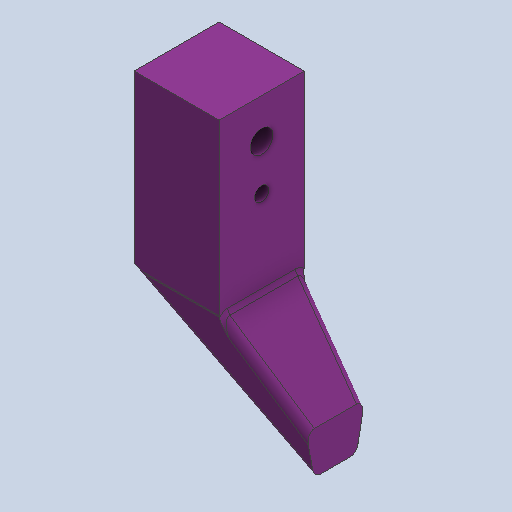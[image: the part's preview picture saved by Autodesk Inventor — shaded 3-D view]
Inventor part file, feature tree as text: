
AUTODESK INVENTOR PART (.ipt)
format: ipt  version: 2025.1 (Build 291241020, 241B)  size: 309,248 bytes
history: native  units: in
note: dims shown in document units (in); Inventor stores cm internally (conversion verified against a paired STEP export)
features: extrude x4, sketch x4, fillet x1
ambient origin geometry x8: Origin, YZ Plane, XZ Plane, XY Plane, X Axis, Y Axis, Z Axis, Center Point
bodies: Solid1 (feature_tree)
feature tree (9):
  extrude  "Extrusion1"  Depth=1.5in
  extrude  "Extrusion2"  Depth=2.0in
  extrude  "Extrusion3"  Depth=1.5in TaperAngle=0.0deg
  fillet  "Fillet1"  Radius=0.375in
  extrude  "Extrusion4"  Depth=0.125in
  sketch  "Sketch1"  dims[d0=3.0in d1=1.5in]
  sketch  "Sketch3"  dims[d3=2.8in d4=2.0in]
  sketch  "Sketch4"  dims[d5=0.75in d6=1.5in d7=0.0in d9=0.375in]
  sketch  "Sketch5"  dims[d10=1.5in d11=0.0in d12=1.3in d13=0.3976in d14=0.7in d15=1.0in d16=0.0in d17=0.125in d18=0.25in d19=1.5in d20=1.0in d21=0.0in]
